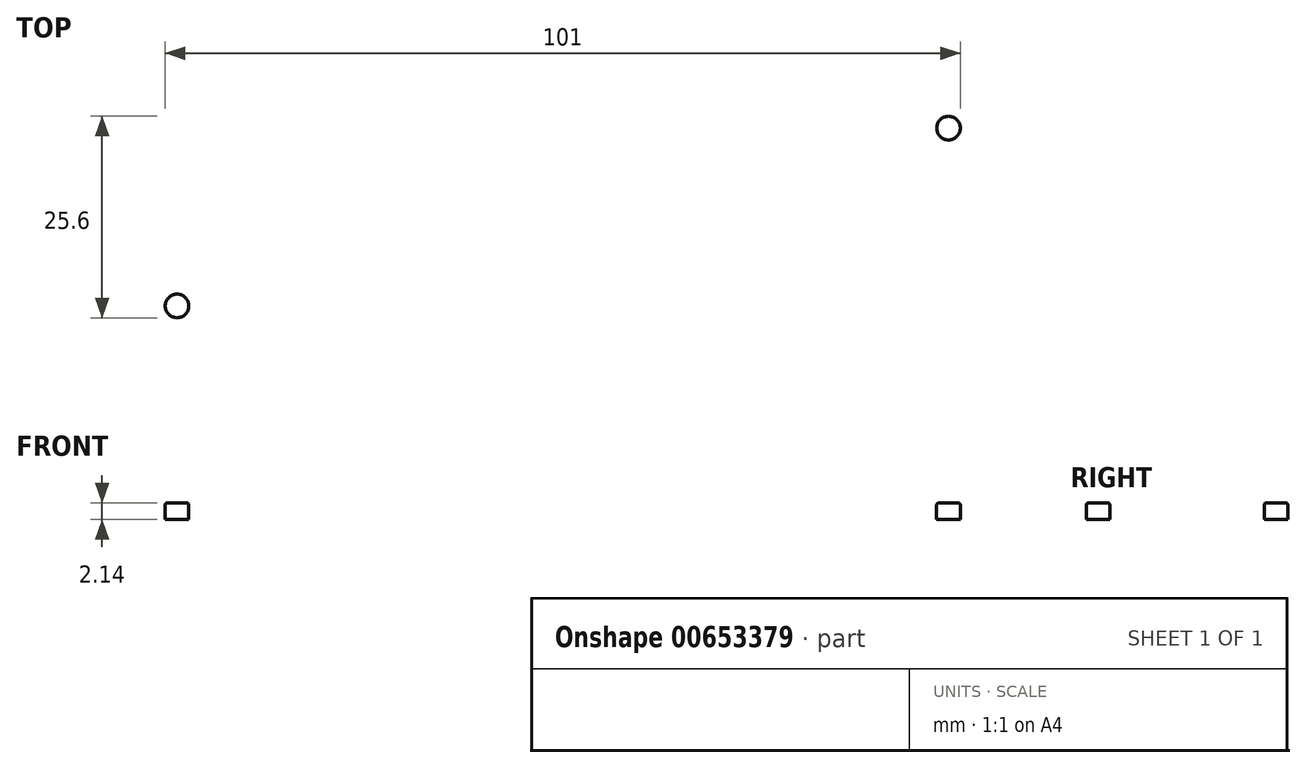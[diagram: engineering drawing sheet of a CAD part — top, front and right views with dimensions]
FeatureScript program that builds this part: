
annotation { "Feature Type Name" : "Feature", "Feature Type Description" : "" }
export const myFeature = defineFeature(function(context is Context, id is Id, definition is map)
    precondition{}
    {
        {
            var Q0;
            Q0=qCreatedBy(makeId("Top.planeOp"),FACE);
            var sketch = newSketch(context, id + "F0", { "sketchPlane" : qUnion([Q0])});
            skLineSegment(sketch, "E0.bottom", {"start": v(52.5, 15) * mm, "end": v(-52.5, 15) * mm});
            skLineSegment(sketch, "E0.top", {"start": v(52.5, -15) * mm, "end": v(-52.5, -15) * mm});
            skLineSegment(sketch, "E0.left", {"start": v(52.5, 15) * mm, "end": v(52.5, -15) * mm});
            skLineSegment(sketch, "E0.right", {"start": v(-52.5, 15) * mm, "end": v(-52.5, -15) * mm});
            skPoint(sketch, "E0.middle", {"position": v(0, 0) * mm});
            skSolve(sketch);
        }
        {
            var Q0;
            Q0=makeQuery(id+"F0.imprint","IMPRINT",FACE,{"disambiguationData":[TD([[makeQuery(id+"F0.imprint","IMPRINT",EDGE,{"derivedFrom":sQuery(id+"F0.wireOp",EDGE,"E0.bottom")}),1.0]])]});
            extrude(context, id + "F1", {"entities" : qUnion([Q0]), "depth" : 2.14 * mm, "offsetDistance" : 25.4 * mm});
        }
        {
            var Q0;
            Q0=makeQuery(id+"F1.opExtrude","SWEPT_EDGE",EDGE,{"disambiguationData":[OSD([sQuery(id+"F0.wireOp",EDGE,"E0.top"),sQuery(id+"F0.wireOp",EDGE,"E0.right")])]});
            var Q1;
            Q1=makeQuery(id+"F1.opExtrude","SWEPT_EDGE",EDGE,{"disambiguationData":[OSD([sQuery(id+"F0.wireOp",EDGE,"E0.bottom"),sQuery(id+"F0.wireOp",EDGE,"E0.right")])]});
            var Q2;
            Q2=makeQuery(id+"F1.opExtrude","SWEPT_EDGE",EDGE,{"disambiguationData":[OSD([sQuery(id+"F0.wireOp",EDGE,"E0.bottom"),sQuery(id+"F0.wireOp",EDGE,"E0.left")])]});
            var Q3;
            Q3=makeQuery(id+"F1.opExtrude","SWEPT_EDGE",EDGE,{"disambiguationData":[OSD([sQuery(id+"F0.wireOp",EDGE,"E0.top"),sQuery(id+"F0.wireOp",EDGE,"E0.left")])]});
            fillet(context, id + "F2", {"entities" : qUnion([Q0, Q1, Q2, Q3]), "radius" : 2.6 * mm, "tangentPropagation" : true, "allowEdgeOverflow" : false});
        }
        {
            var Q0;
            Q0=makeQuery(id+"F1.opExtrude","CAP_FACE",FACE,{"disambiguationData":[OSD([sQuery(id+"F0.wireOp",EDGE,"E0.bottom"),sQuery(id+"F0.wireOp",EDGE,"E0.top"),sQuery(id+"F0.wireOp",EDGE,"E0.left"),sQuery(id+"F0.wireOp",EDGE,"E0.right")])],"isStart":false});
            var sketch = newSketch(context, id + "F3", { "sketchPlane" : qUnion([Q0])});
            skCircle(sketch, "E1", {"center": v(-49, 11.3) * mm, "radius": 1.5 * mm});
            skCircle(sketch, "E2.MirrorC", {"center": v(49, 11.3) * mm, "radius": 1.5 * mm});
            skCircle(sketch, "E3.MirrorC", {"center": v(-49, -11.3) * mm, "radius": 1.5 * mm});
            skCircle(sketch, "E4.MirrorC", {"center": v(49, -11.3) * mm, "radius": 1.5 * mm});
            skSolve(sketch);
        }
        {
            var Q0;
            Q0=makeQuery(id+"F3.imprint","IMPRINT",FACE,{"disambiguationData":[TD([[makeQuery(id+"F3.imprint","IMPRINT",EDGE,{"derivedFrom":sQuery(id+"F3.wireOp",EDGE,"E1")}),1.0]])]});
            var Q1;
            Q1=makeQuery(id+"F3.imprint","IMPRINT",FACE,{"disambiguationData":[TD([[makeQuery(id+"F3.imprint","IMPRINT",EDGE,{"derivedFrom":sQuery(id+"F3.wireOp",EDGE,"E3.MirrorC")}),-1.0]])]});
            var Q2;
            Q2=makeQuery(id+"F3.imprint","IMPRINT",FACE,{"disambiguationData":[TD([[makeQuery(id+"F3.imprint","IMPRINT",EDGE,{"derivedFrom":sQuery(id+"F3.wireOp",EDGE,"E4.MirrorC")}),1.0]])]});
            var Q3;
            Q3=makeQuery(id+"F3.imprint","IMPRINT",FACE,{"disambiguationData":[TD([[makeQuery(id+"F3.imprint","IMPRINT",EDGE,{"derivedFrom":sQuery(id+"F3.wireOp",EDGE,"E2.MirrorC")}),-1.0]])]});
            var Q4;
            Q4=makeQuery(id+"F1.opExtrude","CAP_FACE",FACE,{"disambiguationData":[OSD([sQuery(id+"F0.wireOp",EDGE,"E0.bottom"),sQuery(id+"F0.wireOp",EDGE,"E0.top"),sQuery(id+"F0.wireOp",EDGE,"E0.left"),sQuery(id+"F0.wireOp",EDGE,"E0.right")])],"isStart":true});
            extrude(context, id + "F4", {"entities" : qUnion([Q0, Q1, Q2, Q3]), "operationType" : NewBodyOperationType.REMOVE, "endBound" : BoundingType.UP_TO_SURFACE, "oppositeDirection" : true, "depth" : 25.4 * mm, "endBoundEntityFace" : qUnion([Q4]), "offsetDistance" : 25.4 * mm});
        }
        {
            var Q0;
            Q0=makeQuery(id+"F1.opExtrude","CAP_FACE",FACE,{"disambiguationData":[OSD([sQuery(id+"F0.wireOp",EDGE,"E0.bottom"),sQuery(id+"F0.wireOp",EDGE,"E0.top"),sQuery(id+"F0.wireOp",EDGE,"E0.left"),sQuery(id+"F0.wireOp",EDGE,"E0.right")])],"isStart":false});
            fillet(context, id + "F5", {"entities" : qUnion([Q0]), "radius" : 0.3 * mm, "tangentPropagation" : true, "allowEdgeOverflow" : false});
        }
    });
